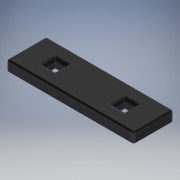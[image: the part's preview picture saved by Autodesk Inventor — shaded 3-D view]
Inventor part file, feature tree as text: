
AUTODESK INVENTOR PART (.ipt)
format: ipt  version: 2018 (Build 220112000, 112)  size: 181,248 bytes
history: native  units: mm
features: extrude x4, sketch x4, fillet x3, projected_geometry x2
ambient origin geometry x8: Origin, YZ Plane, XZ Plane, XY Plane, X Axis, Y Axis, Z Axis, Center Point
bodies: Solid1 (feature_tree)
feature tree (13):
  extrude  "Extrusion1"  Depth=10.0mm
  extrude  "Extrusion2"  Depth=10.2mm
  fillet  "Fillet1"  Radius=10.2mm
  extrude  "Extrusion3"  Depth=10.2mm TaperAngle=0.0deg
  extrude  "Extrusion4"  Depth=2.0mm
  fillet  "Fillet2"  Radius=8.0mm
  fillet  "Fillet3"  Radius=8.0mm
  sketch  "Sketch1"  dims[d0=10.0mm d1=0.0mm d4=30.0mm]
  sketch  "Sketch2"  dims[d5=60.0mm d6=5.1mm d7=10.2mm]
  sketch  "Sketch4"  dims[d8=10.2mm d9=100.0mm d10=0.0mm]
  projected_geometry  "Projected Loop1"
  sketch  "Sketch5"  dims[d12=2.0mm d13=2.8mm d14=8.0mm d15=0.0mm d16=8.0mm d17=0.0mm d18=4.0mm d19=2.0mm]
  projected_geometry  "Projected Loop2"
